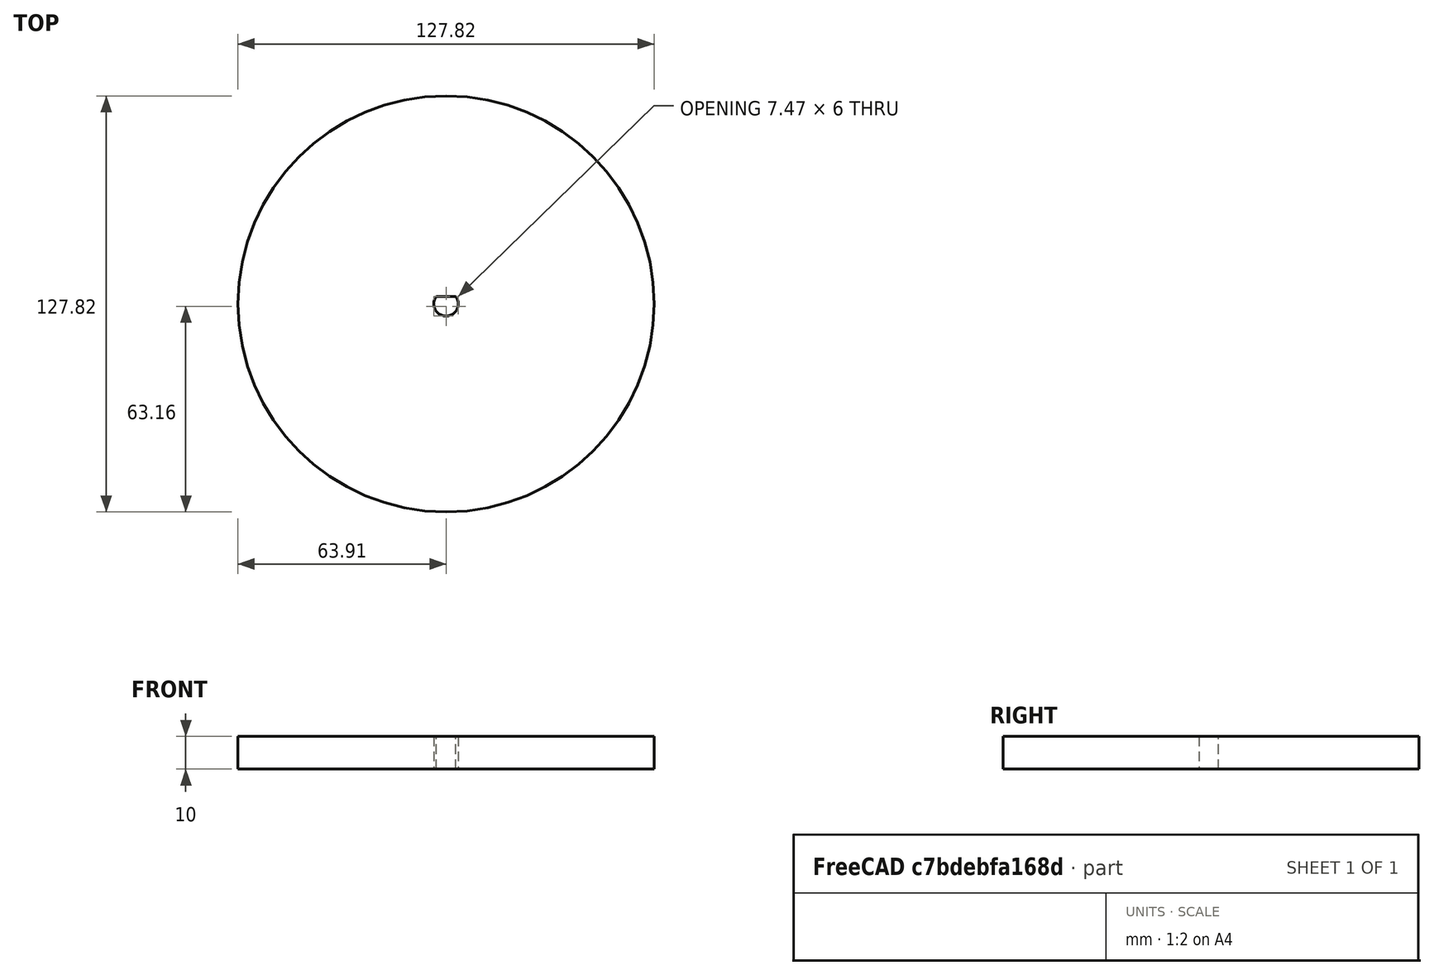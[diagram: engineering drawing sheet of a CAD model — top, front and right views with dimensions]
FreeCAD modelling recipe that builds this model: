
FCSTD DOCUMENT  (FreeCAD 0.18R14555 (Git shallow))
Label: Bottom
License: All rights reserved
LicenseURL: http://en.wikipedia.org/wiki/All_rights_reserved
objects: PartDesign::Line×5, PartDesign::ShapeBinder×2, Part::Feature×1, Sketcher::SketchObject×1, PartDesign::Pad×1, PartDesign::Body×1
note: 12 computed .brp shape members not serialized (recipe doc carries the construction recipe); baked Part::Feature solids carry a one-line shape summary decoded from their .brp

FEATURE [Part::Feature] Shape  label="ArduinoDXF"
  Placement = pos=(46,16,0) rot=(0,0,1;1.5708rad)
  shape: bbox 75.08 x 53.34 x 2e-07 mm, 0 faces, 0 solids (baked)
FEATURE [PartDesign::Line] DatumLine
  AttacherType = Attacher::AttachEngineLine
  MapMode = 29
  Placement = pos=(46,16,0) rot=(0.57735,-0.57735,-0.57735;2.0944rad)
FEATURE [PartDesign::Line] DatumLine001
  AttacherType = Attacher::AttachEngineLine
  MapMode = 29
  Placement = pos=(46,-37.34,0) rot=(0.57735,0.57735,0.57735;2.0944rad)
FEATURE [PartDesign::ShapeBinder] ReferenceShape
  Placement = pos=(46,16,0) rot=(0,0,1;1.5708rad)
  Support = -> [Shape]
  TraceSupport = false
FEATURE [PartDesign::ShapeBinder] ReferenceShape001
  Placement = pos=(46,16,0) rot=(0,0,1;1.5708rad)
  Support = -> [Shape]
  TraceSupport = false
FEATURE [PartDesign::Line] DatumLine002
  AttacherType = Attacher::AttachEngineLine
  MapMode = 29
  Placement = pos=(-22.58,16,0) rot=(0,0.707107,0.707107;3.14159rad)
  Support = -> [ReferenceShape,ReferenceShape001]
FEATURE [PartDesign::Line] DatumLine003
  AttacherType = Attacher::AttachEngineLine
  MapMode = 29
  Placement = pos=(46,16,0) rot=(0,0.707107,0.707107;3.14159rad)
FEATURE [PartDesign::Line] DatumLine004
  AttacherType = Attacher::AttachEngineLine
  MapMode = 29
  Placement = pos=(52.5024,16,0) rot=(1,0,0;1.5708rad)
  Support = -> [Shape]
FEATURE [Sketcher::SketchObject] Sketch
  ExternalGeometry = -> [DatumLine,DatumLine001,DatumLine002,DatumLine003,DatumLine004]
  MapMode = 5
  Support = -> [XY_Plane]
  expr: Constraints[2] = 6.5 + 1
  sketch-geometry (7):
    g0: ArcOfCircle CenterX=-1.08 CenterY=-2.5 CenterZ=0 NormalX=0 NormalY=0 NormalZ=1 AngleXU=0 Radius=3.75 StartAngle=2.49809 EndAngle=6.92669
    g1: LineSegment [constr] StartX=-4.14 StartY=-6.25 StartZ=0 EndX=4.14 EndY=-6.25 EndZ=0
    g2: LineSegment StartX=-4.08 StartY=-0.25 StartZ=0 EndX=1.92 EndY=-0.25 EndZ=0
    g3: GeomPoint X=0 Y=16 Z=0
    g4: Circle CenterX=-1.08 CenterY=-2.5 CenterZ=0 NormalX=0 NormalY=0 NormalZ=1 AngleXU=0 Radius=63.9132
    g5: GeomPoint X=52.5024 Y=-37.34 Z=0
    g6: GeomPoint X=-22.58 Y=16 Z=0
  constraints (19):
    c: Tangent(g1,g0)
    c: Horizontal(g2)
    c: Diameter(g0) = 7.5
    c: PointOnObject(g3,g-3)
    c: PointOnObject(g3,g-2)
    c: DistanceY(g0,g3) = 18.5
    c: Coincident(g0,g2)
    c: Coincident(g0,g2)
    c: Coincident(g0,g2)
    c: DistanceY(g1,g0) = 6
    c: Coincident(g4,g0)
    c: PointOnObject(g5,g4)
    c: PointOnObject(g5,g-4)
    c: PointOnObject(g5,g-7)
    c: PointOnObject(g6,g-5)
    c: PointOnObject(g6,g-3)
    c: DistanceX(g6,g0) = 21.5
    c: DistanceX(g1,g-1) = 4.14
    c: Symmetric(g1,g1,g-2)
FEATURE [PartDesign::Pad] Pad
  Length = 10
  Length2 = 100
  Profile = -> Sketch
  Type = 0
FEATURE [PartDesign::Body] Body
  Group = -> [Sketch,DatumLine,DatumLine001,DatumLine002,ReferenceShape,ReferenceShape001,DatumLine003,DatumLine004,Pad]
  Origin = -> Origin
  Tip = -> Pad
